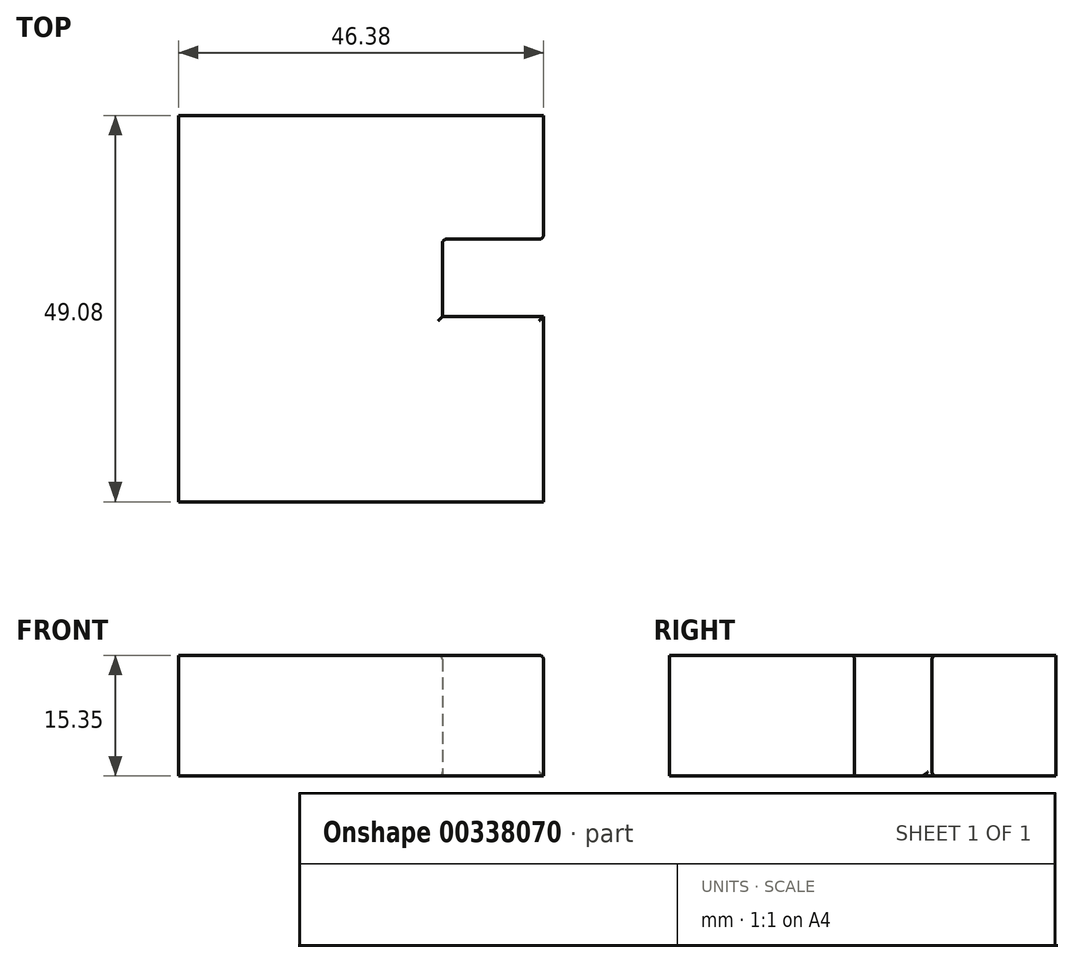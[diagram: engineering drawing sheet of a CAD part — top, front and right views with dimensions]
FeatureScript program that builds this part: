
annotation { "Feature Type Name" : "Feature", "Feature Type Description" : "" }
export const myFeature = defineFeature(function(context is Context, id is Id, definition is map)
    precondition{}
    {
        {
            var Q0;
            Q0=qCreatedBy(makeId("Top.planeOp"),FACE);
            var sketch = newSketch(context, id + "F0", { "sketchPlane" : qUnion([Q0])});
            skLineSegment(sketch, "E0.bottom", {"start": v(-46.38, -33.36) * mm, "end": v(0, -33.36) * mm});
            skLineSegment(sketch, "E0.top", {"start": v(-46.38, 15.72) * mm, "end": v(0, 15.72) * mm});
            skLineSegment(sketch, "E0.left", {"start": v(-46.38, -33.36) * mm, "end": v(-46.38, 15.72) * mm});
            skLineSegment(sketch, "E0.right", {"start": v(0, -33.36) * mm, "end": v(0, 15.72) * mm});
            skLineSegment(sketch, "E1.bottom", {"start": v(-12.85, -9.84) * mm, "end": v(0, -9.84) * mm});
            skLineSegment(sketch, "E1.top", {"start": v(-12.85, 0) * mm, "end": v(0, 0) * mm});
            skLineSegment(sketch, "E1.left", {"start": v(-12.85, -9.84) * mm, "end": v(-12.85, 0) * mm});
            skLineSegment(sketch, "E1.right", {"start": v(0, -9.84) * mm, "end": v(0, 0) * mm});
            skSolve(sketch);
        }
        {
            var Q0;
            {var subQ1=sQuery(id+"F0.wireOp",EDGE,"E0.bottom");Q0=makeQuery(id+"F0.imprint","IMPRINT",FACE,{"disambiguationData":[TD([[makeQuery(id+"F0.imprint","IMPRINT",EDGE,{"derivedFrom":subQ1}),1.0]])]});}
            extrude(context, id + "F1", {"entities" : qUnion([Q0]), "depth" : 15.35 * mm});
        }
        {
            var Q0;
            {var subQ0=sQuery(id+"F0.wireOp",EDGE,"E0.right");Q0=makeQuery(id+"F1.opExtrude","CAP_EDGE",EDGE,{"disambiguationData":[OSD([subQ0]),TDD([makeQuery(id+"F0.imprint","IMPRINT",EDGE,{"disambiguationData":[TD([[makeQuery(id+"F0.imprint","INTERSECT",VERTEX,{"derivedFrom":[sQuery(id+"F0.wireOp",EDGE,"E0.bottom"),subQ0]}),-1.0]])],"derivedFrom":subQ0})])],"isStart":false});}
            var Q1;
            {var subQ0=sQuery(id+"F0.wireOp",EDGE,"E0.right");Q1=makeQuery(id+"F1.opExtrude","CAP_EDGE",EDGE,{"disambiguationData":[OSD([subQ0]),TDD([makeQuery(id+"F0.imprint","IMPRINT",EDGE,{"disambiguationData":[TD([[makeQuery(id+"F0.imprint","INTERSECT",VERTEX,{"derivedFrom":[sQuery(id+"F0.wireOp",EDGE,"E0.top"),subQ0]}),1.0]])],"derivedFrom":subQ0})])],"isStart":false});}
            var Q2;
            Q2=makeQuery(id+"F1.opExtrude","CAP_EDGE",EDGE,{"disambiguationData":[OSD([sQuery(id+"F0.wireOp",EDGE,"E1.left")])],"isStart":false});
            var Q3;
            Q3=makeQuery(id+"F1.opExtrude","CAP_EDGE",EDGE,{"disambiguationData":[OSD([sQuery(id+"F0.wireOp",EDGE,"E1.bottom")])],"isStart":false});
            var Q4;
            Q4=makeQuery(id+"F1.opExtrude","SWEPT_FACE",FACE,{"disambiguationData":[OSD([sQuery(id+"F0.wireOp",EDGE,"E1.top")])]});
            fillet(context, id + "F2", {"entities" : qUnion([Q0, Q1, Q2, Q3, Q4]), "radius" : 0.54 * mm, "tangentPropagation" : true, "allowEdgeOverflow" : false});
        }
    });
